# Revit family: MTXTYP010
name_source: partatom
category: Furniture
units: mm (PartAtom-declared; Revit-internal decimal feet)

## family parameters
Always vertical = Yes
Cut with Voids When Loaded = No
OmniClass Number = 23.40.20.00
OmniClass Title = General Furniture and Specialties
Render Appearance Source = Family Geometry
Room Calculation Point = No
Shared = No
Work Plane-Based = No

## types (1)
- MTXTYP010
    Cost = 114477 $
    Default Elevation = 0 mm  [stored 0 ft]
    Description = 1 x 69 in. Electrical Jumper  (Pt 48E), 2 x Matrix White Duplex Outlet - Line 1, 3 x Matrix White Duplex Outlet - Line 2, 3 x Matrix White Duplex Outlet - Line 3, 3 x Matrix White Duplex Outlet - Line 4 - Dedicated, 1 x 18 in. Electrical Jumper  (Panel To Panel), 1 x 21 in. Electrical Jumper  (Extended Panel To Panel), 4 x Single Powerway Assembly - 48W - 8 wire, 4 circuit, 7 x Access Hole Cover, 1 x LH Receptacle Mounted Base Infeed - 72L - 8 Wire, 4 Circuit, 6 x Desking L-Bracket Pair - Black, 1 x Dual Electrical Tile - 8H X 48W, 11 x Quad Electrical Tile - 8H X 48W, 8 x MX Monolithic Laminate Tile Single Sided 48H X 36W, 12 x Tackable Acoustical Tile - 40H x 48W, 36 x Tackable Acoustical Tile - 48H x 36W, 2 x 3-Way  90 Degree Connector - Linear Trim - 50H, 6 x 2-Way 90 Degree Connector - Linear Trim - 50H, 8 x MATRIX LINEAR Double Frame Recessed Glass Kit 36" & 36", 3 x MATRIX LINEAR Double Frame Recessed Glass Kit 48" & 48", 8 x Frame End Cap - Linear Trim - 50H, 22 x Panel Frame - Linear Trim - 50H x 36W, 6 x Panel Frame - Linear Trim - 50H x 48W, 8 x MATRIX RECESSED FRAMELESS GLASS 8"H X 72"W V2, 3 x MATRIX RECESSED FRAMELESS GLASS 8"H X 96"W V2, 2 x 4-Way 90 Degree Connector - Linear Trim - 50H, 6 x TBL, REC, 2MM, 30DX72WX29H, HAL, E SERIES GLD 2 STAGE, 6 x Rectangular - 2mm Edge - 24D x 54W, 3 x Regular Cantilever - Left Hand - 24D, 3 x Regular Cantilever - Right Hand - 24D, 6 x Cbx Partial Depth Bbf Ped 23dx28hx16w, 3 x Cbx Single Door Tower Hinge Left 24dx50hx12w, 3 x Cbx Single Door Tower Hinge Right 24dx50hx12w
    Exported From CET Designer = Yes
    Manufacturer = AIS
    Model = E-MW8W4PJ48E
    Show MTXTYP010 = Yes
    VisibilityIndex = 0

note: [stored X ft] marks values corroborated as IEEE doubles in the binary element streams (Revit-internal decimal feet)

## geometry (parser evidence)
native form markers: Sweep x2
no freeform markers — native parametric forms only
